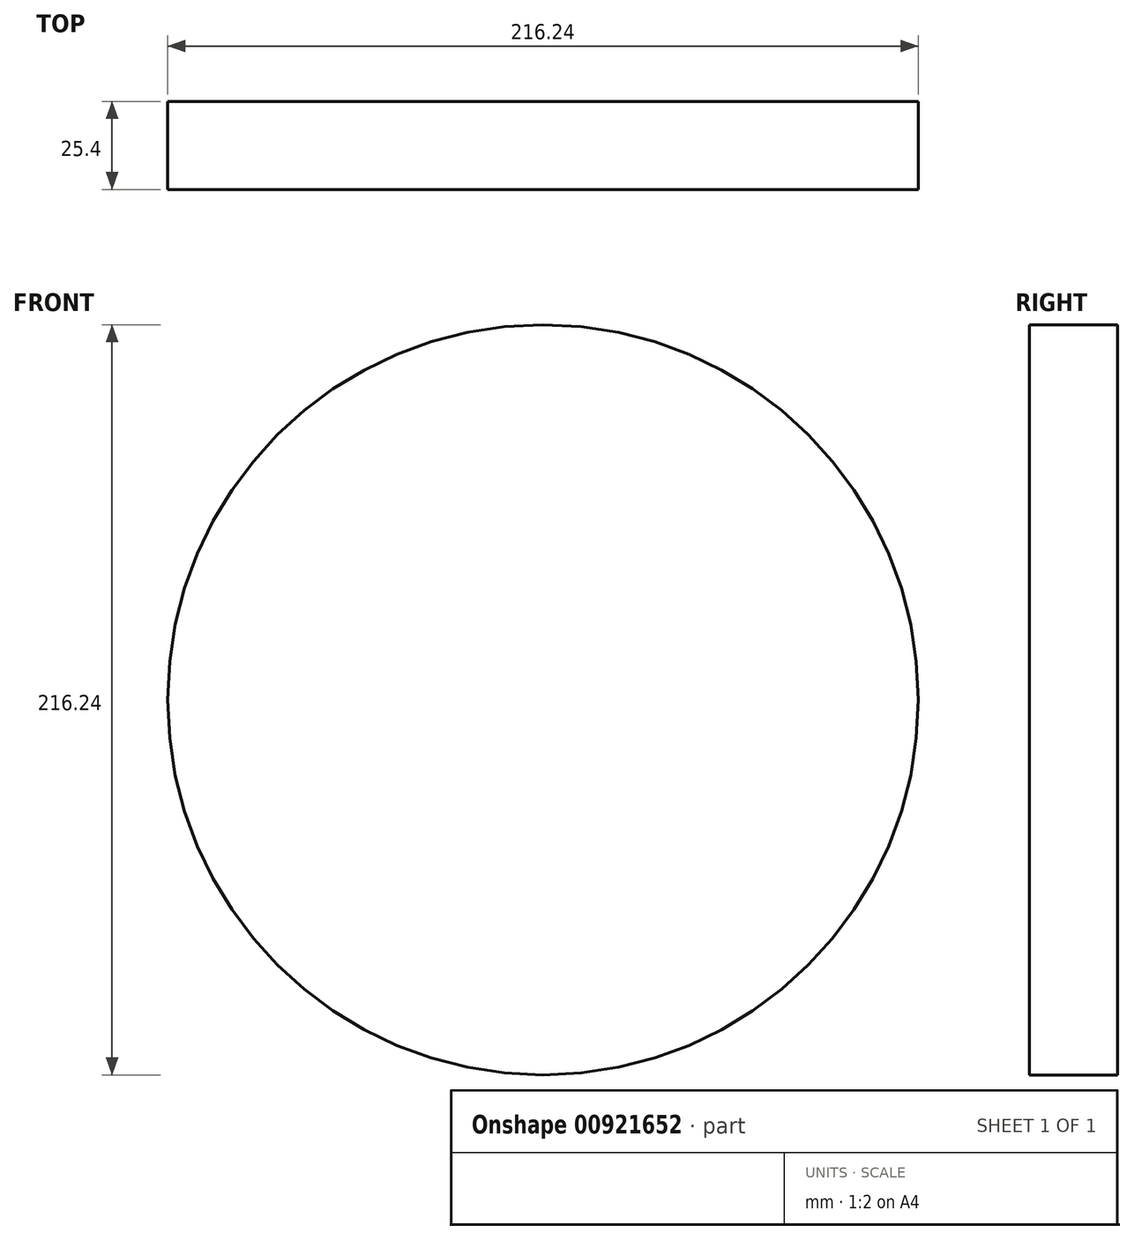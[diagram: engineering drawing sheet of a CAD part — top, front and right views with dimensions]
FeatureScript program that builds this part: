
annotation { "Feature Type Name" : "Feature", "Feature Type Description" : "" }
export const myFeature = defineFeature(function(context is Context, id is Id, definition is map)
    precondition{}
    {
        {
            var Q0;
            Q0=qCreatedBy(makeId("Front.planeOp"),FACE);
            var sketch = newSketch(context, id + "F0", { "sketchPlane" : qUnion([Q0])});
            skLineSegment(sketch, "E0", {"start": v(-57.09, 32.52) * mm, "end": v(67.3, 32.52) * mm});
            skLineSegment(sketch, "E1", {"start": v(67.3, 32.52) * mm, "end": v(0.91, -0.37) * mm});
            skLineSegment(sketch, "E2", {"start": v(0.91, -0.37) * mm, "end": v(-57.09, 32.52) * mm});
            skSolve(sketch);
        }
        {
            var Q0;
            Q0=sQuery(id+"F0.wireOp",EDGE,"E1");
            var Q1;
            Q1=sQuery(id+"F0.wireOp",EDGE,"E0");
            var Q2;
            Q2=sQuery(id+"F0.wireOp",EDGE,"E2");
            extrude(context, id + "F1", {"bodyType" : ToolBodyType.SURFACE, "surfaceEntities" : qUnion([Q0, Q1, Q2]), "depth" : 25.4 * mm, "offsetDistance" : 25.4 * mm});
        }
        {
            var Q0;
            Q0=qCreatedBy(makeId("Front.planeOp"),FACE);
            var sketch = newSketch(context, id + "F2", { "sketchPlane" : qUnion([Q0])});
            skCircle(sketch, "E3", {"center": v(0, -82.82) * mm, "radius": 108.12 * mm});
            skSolve(sketch);
        }
        {
            var Q0;
            Q0=makeQuery(id+"F2.imprint","IMPRINT",FACE,{"disambiguationData":[TD([[makeQuery(id+"F2.imprint","IMPRINT",EDGE,{"derivedFrom":sQuery(id+"F2.wireOp",EDGE,"E3")}),1.0]])]});
            extrude(context, id + "F3", {"entities" : qUnion([Q0]), "depth" : 25.4 * mm, "offsetDistance" : 25.4 * mm});
        }
    });
